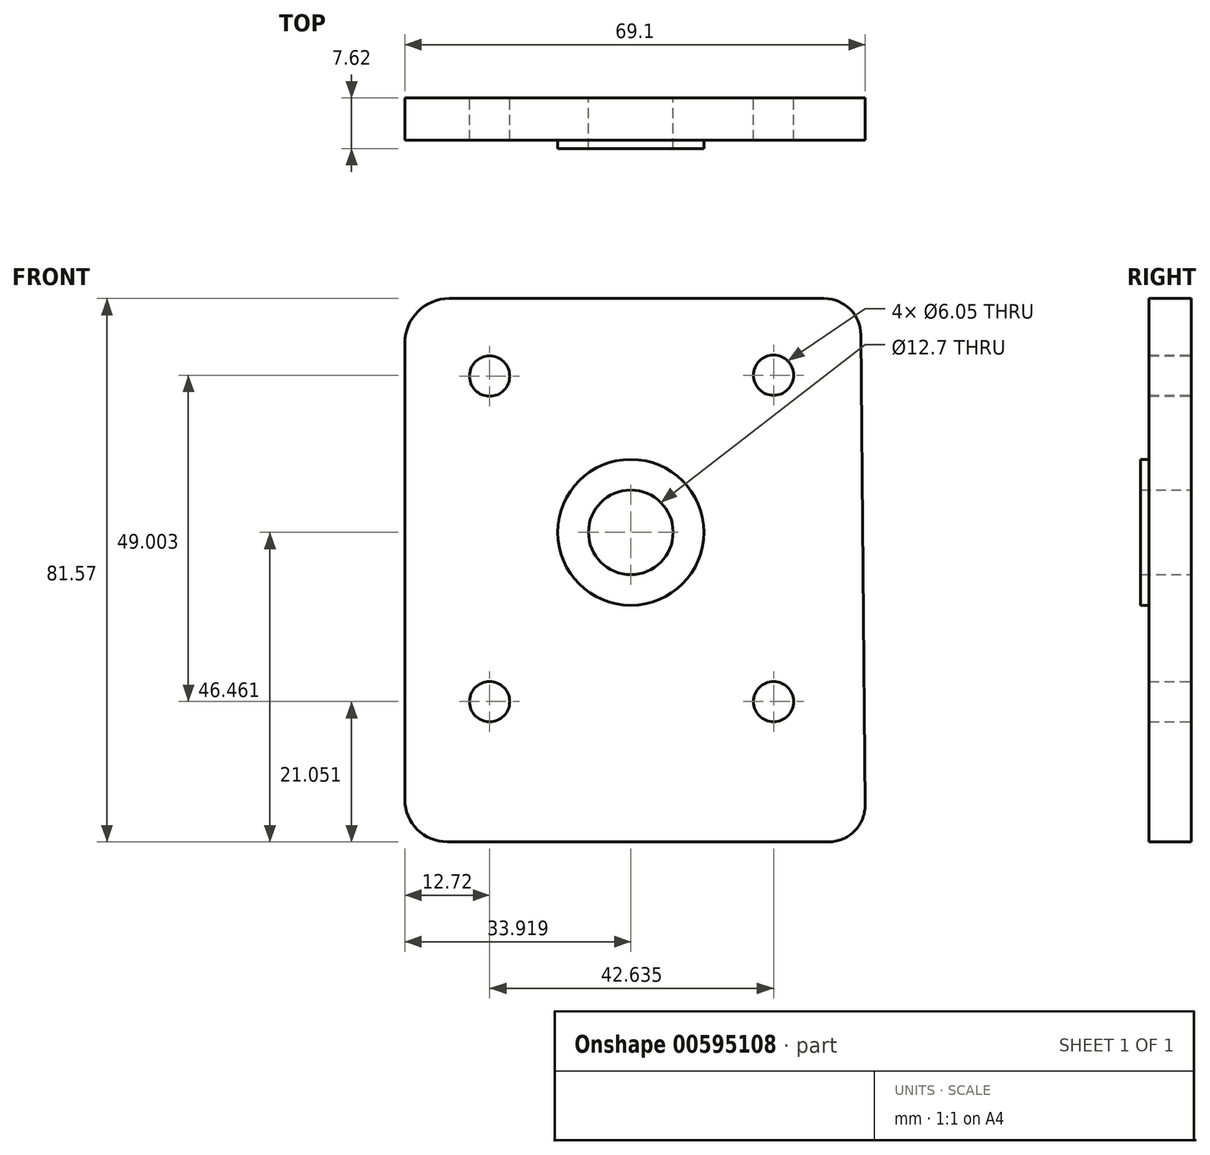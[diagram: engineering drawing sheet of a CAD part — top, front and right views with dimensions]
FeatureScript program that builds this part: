
annotation { "Feature Type Name" : "Feature", "Feature Type Description" : "" }
export const myFeature = defineFeature(function(context is Context, id is Id, definition is map)
    precondition{}
    {
        {
            var Q0;
            Q0=qCreatedBy(makeId("Front.planeOp"),FACE);
            var sketch = newSketch(context, id + "F0", { "sketchPlane" : qUnion([Q0])});
            skLineSegment(sketch, "E0.top", {"start": v(50.88, 55.27) * mm, "end": v(-6.37, 55.27) * mm});
            skPoint(sketch, "E1.middle", {"position": v(-12.72, 55.27) * mm});
            skLineSegment(sketch, "E2.top", {"start": v(-6.04, 136.84) * mm, "end": v(50.24, 136.84) * mm});
            skLineSegment(sketch, "E2.left", {"start": v(-12.72, 61.62) * mm, "end": v(-12.72, 130.15) * mm});
            skLineSegment(sketch, "E2.right", {"start": v(56.38, 60.81) * mm, "end": v(55.74, 131.4) * mm});
            skCircle(sketch, "E3", {"center": v(0, 125.19) * mm, "radius": 3.02 * mm});
            skCircle(sketch, "E4", {"center": v(42.64, 76.32) * mm, "radius": 3.02 * mm});
            skCircle(sketch, "E5", {"center": v(0, 76.32) * mm, "radius": 3.02 * mm});
            skCircle(sketch, "E6", {"center": v(42.64, 125.32) * mm, "radius": 3.02 * mm});
            skPoint(sketch, "E7.visualSharp", {"position": v(55.69, 136.84) * mm});
            skPoint(sketch, "E8.visualSharp", {"position": v(-12.72, 136.84) * mm});
            skArc(sketch, "E8.filletArc", {"start": v(-6.04, 136.84) * mm, "mid": v(-10.76, 134.88) * mm, "end": v(-12.72, 130.15) * mm});
            skPoint(sketch, "E9.visualSharp", {"position": v(56.43, 55.27) * mm});
            skArc(sketch, "E10.filletArc", {"start": v(55.74, 131.4) * mm, "mid": v(54.1, 135.25) * mm, "end": v(50.24, 136.84) * mm});
            skArc(sketch, "E11.filletArc", {"start": v(50.88, 55.27) * mm, "mid": v(54.79, 56.9) * mm, "end": v(56.38, 60.81) * mm});
            skCircle(sketch, "E12", {"center": v(21.2, 101.73) * mm, "radius": 6.35 * mm});
            skArc(sketch, "E13.filletArc", {"start": v(-12.72, 61.62) * mm, "mid": v(-10.86, 57.13) * mm, "end": v(-6.37, 55.27) * mm});
            skCircle(sketch, "E14", {"center": v(21.2, 101.73) * mm, "radius": 10.96 * mm});
            skSolve(sketch);
        }
        {
            var Q0;
            Q0=makeQuery(id+"F0.imprint","IMPRINT",FACE,{"disambiguationData":[TD([[makeQuery(id+"F0.imprint","IMPRINT",EDGE,{"derivedFrom":sQuery(id+"F0.wireOp",EDGE,"E0.top")}),-1.0]])]});
            extrude(context, id + "F1", {"entities" : qUnion([Q0]), "depth" : 6.35 * mm, "offsetDistance" : 25.4 * mm});
        }
        {
            var Q0;
            Q0=makeQuery(id+"F0.imprint","IMPRINT",FACE,{"disambiguationData":[TD([[makeQuery(id+"F0.imprint","IMPRINT",EDGE,{"derivedFrom":sQuery(id+"F0.wireOp",EDGE,"E12")}),-1.0]])]});
            extrude(context, id + "F2", {"entities" : qUnion([Q0]), "operationType" : NewBodyOperationType.ADD, "depth" : 7.62 * mm, "offsetDistance" : 25.4 * mm});
        }
    });
